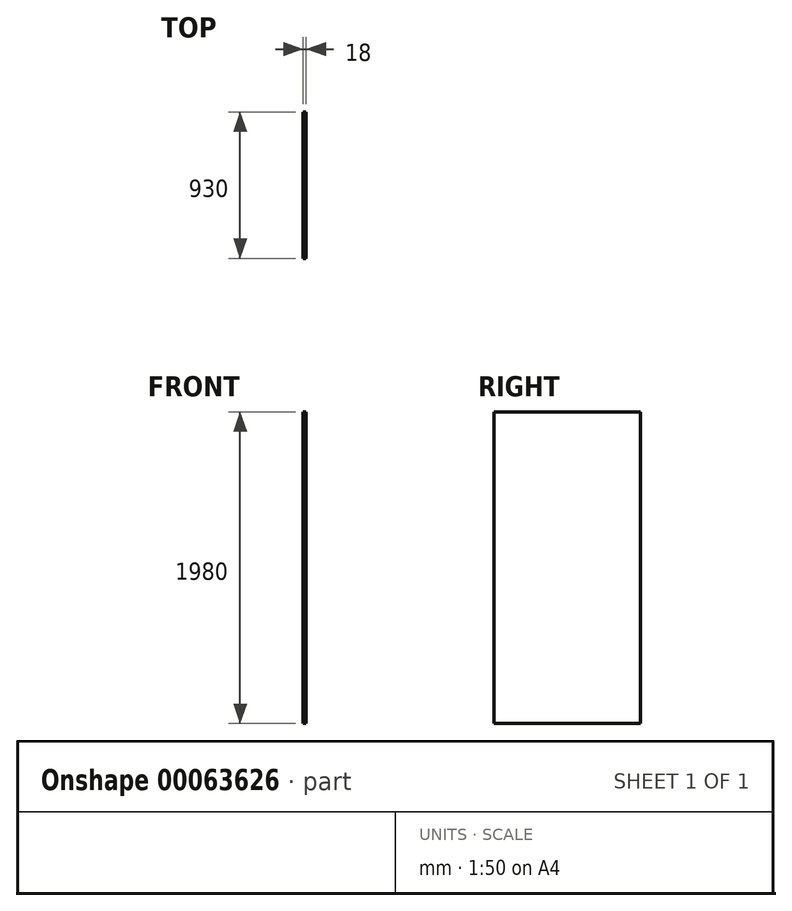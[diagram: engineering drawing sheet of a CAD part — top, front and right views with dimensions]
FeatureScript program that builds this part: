
annotation { "Feature Type Name" : "Feature", "Feature Type Description" : "" }
export const myFeature = defineFeature(function(context is Context, id is Id, definition is map)
    precondition{}
    {
        {
            var Q0;
            Q0=qCreatedBy(makeId("Right.planeOp"),FACE);
            var sketch = newSketch(context, id + "F0", { "sketchPlane" : qUnion([Q0])});
            skLineSegment(sketch, "E0.bottom", {"start": v(0, 0) * mm, "end": v(930, 0) * mm});
            skLineSegment(sketch, "E0.top", {"start": v(0, -1980) * mm, "end": v(930, -1980) * mm});
            skLineSegment(sketch, "E0.left", {"start": v(0, 0) * mm, "end": v(0, -1980) * mm});
            skLineSegment(sketch, "E0.right", {"start": v(930, 0) * mm, "end": v(930, -1980) * mm});
            skSolve(sketch);
        }
        {
            var Q0;
            Q0=makeQuery(id+"F0.imprint","IMPRINT",FACE,{"disambiguationData":[TD([[makeQuery(id+"F0.imprint","IMPRINT",EDGE,{"derivedFrom":sQuery(id+"F0.wireOp",EDGE,"E0.bottom")}),-1.0]])]});
            extrude(context, id + "F1", {"entities" : qUnion([Q0]), "depth" : 18 * mm});
        }
    });
